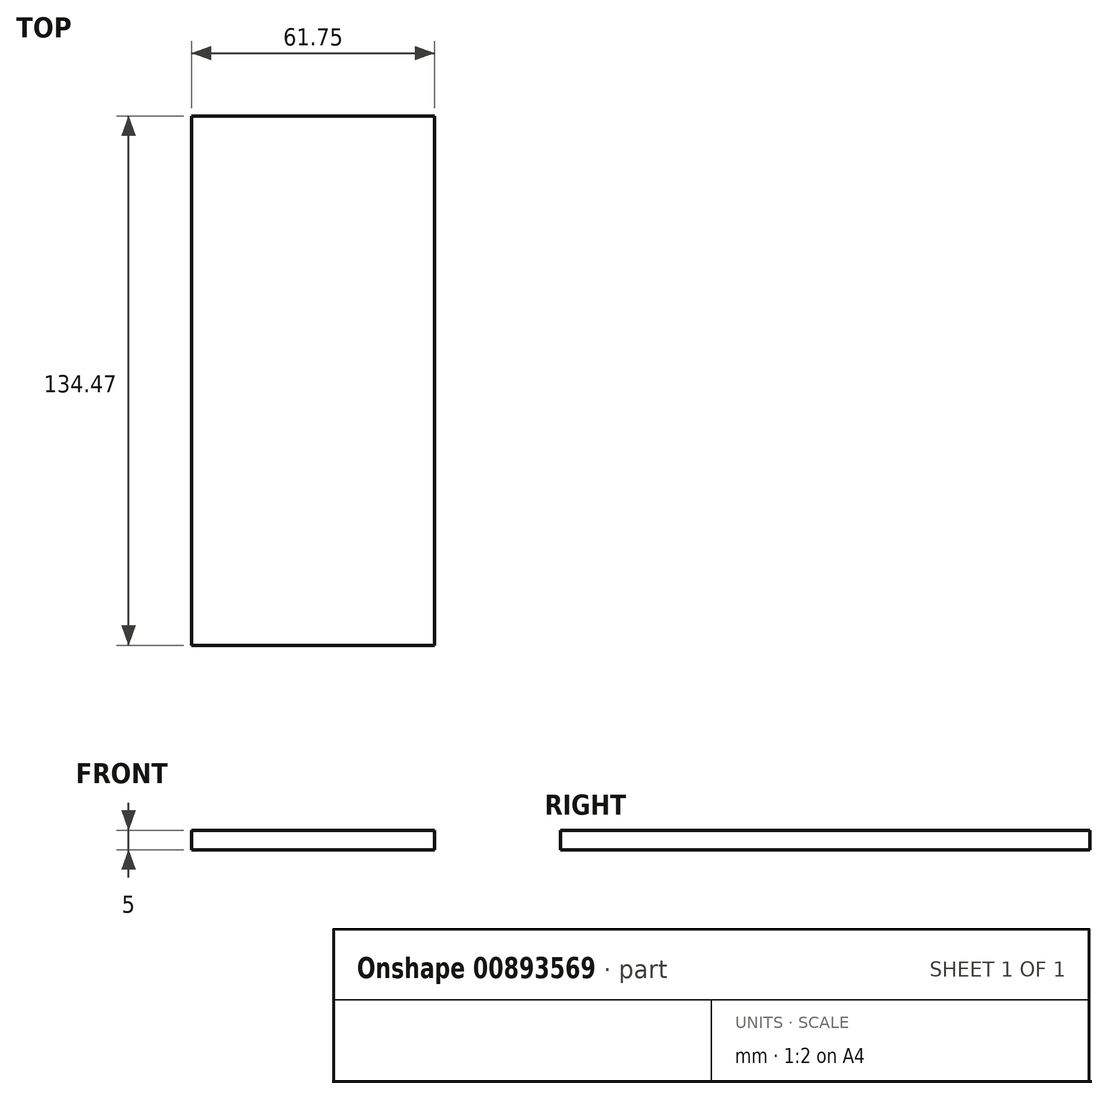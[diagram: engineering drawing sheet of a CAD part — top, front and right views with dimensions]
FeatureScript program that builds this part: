
annotation { "Feature Type Name" : "Feature", "Feature Type Description" : "" }
export const myFeature = defineFeature(function(context is Context, id is Id, definition is map)
    precondition{}
    {
        {
            var Q0;
            Q0=qCreatedBy(makeId("Top.planeOp"),FACE);
            var sketch = newSketch(context, id + "F0", { "sketchPlane" : qUnion([Q0])});
            skLineSegment(sketch, "E0.bottom", {"start": v(-29.1, 59.2) * mm, "end": v(32.64, 59.2) * mm});
            skLineSegment(sketch, "E0.top", {"start": v(-29.1, -75.28) * mm, "end": v(32.64, -75.28) * mm});
            skLineSegment(sketch, "E0.left", {"start": v(-29.1, 59.2) * mm, "end": v(-29.1, -75.28) * mm});
            skLineSegment(sketch, "E0.right", {"start": v(32.64, 59.2) * mm, "end": v(32.64, -75.28) * mm});
            skSolve(sketch);
        }
        {
            var Q0;
            Q0 = qSketchRegion(id + "F0", true);
            extrude(context, id + "F1", {"entities" : qUnion([Q0]), "depth" : 5 * mm, "offsetDistance" : 25 * mm});
        }
    });
